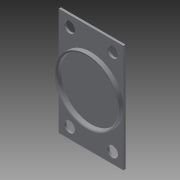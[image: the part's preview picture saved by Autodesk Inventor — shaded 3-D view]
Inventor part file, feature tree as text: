
AUTODESK INVENTOR PART (.ipt)
format: ipt  version: 2014 (Build 180170000, 170)  size: 119,808 bytes
history: native  units: mm
features: extrude x2, fillet x2, sketch x1
ambient origin geometry x8: Origin, YZ Plane, XZ Plane, XY Plane, X Axis, Y Axis, Z Axis, Center Point
bodies: Solid1 (feature_tree)
feature tree (5):
  sketch  "Sketch1"  dims[d0=30.0mm d1=50.0mm d2=5.0mm d3=5.0mm d4=5.0mm d5=5.0mm d6=5.0mm d7=30.0mm d8=28.0mm d9=1.0mm d10=0.0mm d11=3.0mm d12=0.0mm d13=1.0mm d14=1.0mm]
  extrude  "Extrusion1"  Depth=50.0mm
  extrude  "Extrusion2"  Depth=1.0mm
  fillet  "Fillet1"  Radius=5.0mm
  fillet  "Fillet2"  Radius=5.0mm
